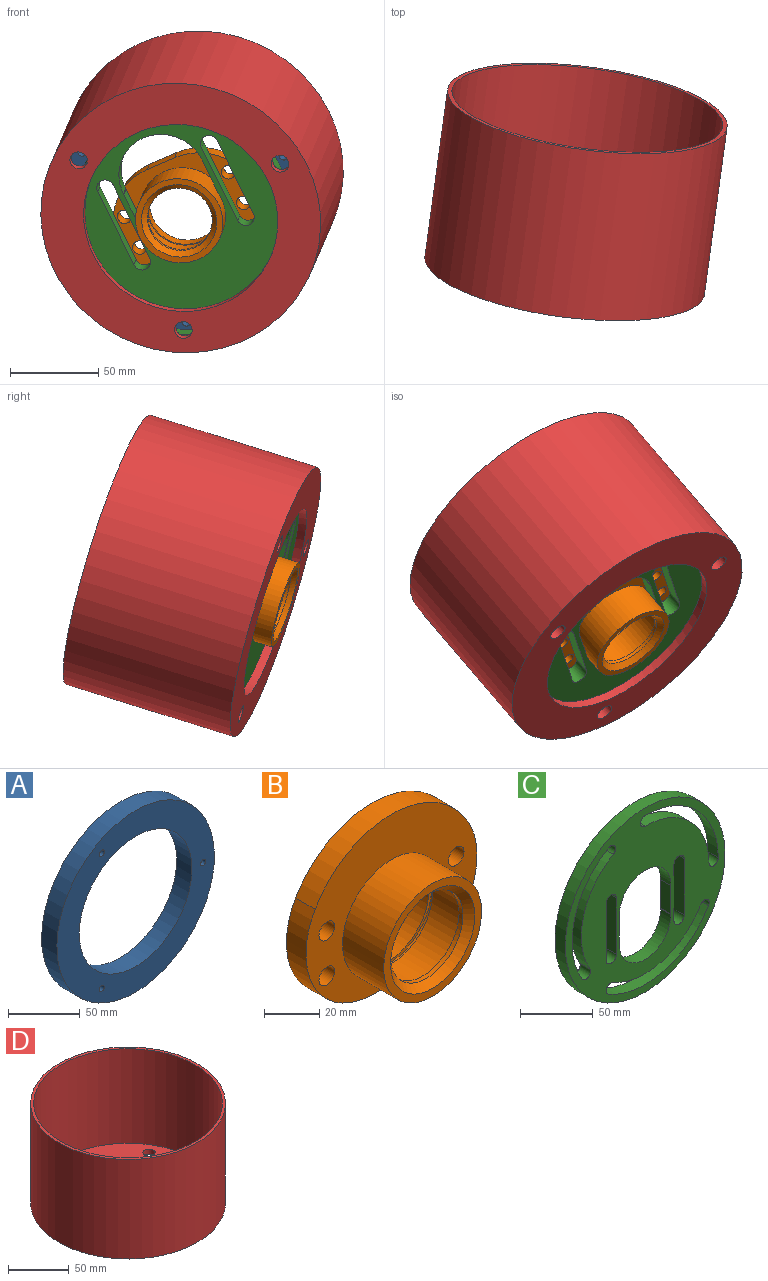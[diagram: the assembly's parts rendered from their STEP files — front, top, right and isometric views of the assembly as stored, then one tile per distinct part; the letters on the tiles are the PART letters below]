
ASSEMBLY  parts=4 mates=4
PART A: 7 faces, bbox 155x15x155 mm
  f0: cylinder r=55.5mm len=111mm, axis (0,1,0), area 5230.8mm2, adj f2,f3
  f1: cylinder r=77.5mm len=155mm, axis (0,1,0), area 7304.2mm2, adj f2,f3
  f2: plane 155x155mm, normal (0,-1,0), area 9133.4mm2, adj f0,f1,f4,f5,f6
  f3: plane 155x155mm, normal (0,1,0), area 9133.4mm2, adj f0,f1,f4,f5,f6
  f4: cylinder r=2.5mm len=15mm, axis (0,1,0), area 235.6mm2, adj f2,f3
  f5: cylinder r=2.5mm len=15mm, axis (0,1,0), area 235.6mm2, adj f2,f3
  f6: cylinder r=2.5mm len=15mm, axis (0,1,0), area 235.6mm2, adj f2,f3
PART B: 20 faces, bbox 87.3x31x75 mm
  f0: plane 87.32x75mm, normal (0,1,0), area 3662.6mm2, adj f1,f11,f12,f13,f14,f15,f17,f18
  f1: cylinder r=45mm len=77.94mm, axis (0,-1,0), area 942.4mm2, adj f0,f2,f18,f19
  f2: plane 87.32x75mm, normal (0,-1,0), area 3084.5mm2, adj f1,f5,f12,f13,f14,f15,f17,f18
  f3: plane 44.5x44.5mm, normal (0,1,0), area 169.8mm2, adj f4,f9
  f4: cylinder r=21mm len=42mm, axis (0,1,0), area 2111.2mm2, adj f3,f6
  f5: cylinder r=25mm len=50mm, axis (0,1,0), area 3298.7mm2, adj f2,f8
  f6: plane 42x42mm, normal (0,1,0), area 310.2mm2, adj f4,f7
  f7: cylinder r=18.5mm len=37mm, axis (0,1,0), area 232.5mm2, adj f6,f16
  f8: plane 50x50mm, normal (0,-1,0), area 511.3mm2, adj f5,f16
  f9: cylinder r=22.25mm len=44.5mm, axis (0,-1,0), area 258.6mm2, adj f3,f10
  f10: plane 44.5x44.5mm, normal (0,-1,0), area 169.8mm2, adj f9,f11
  f11: cylinder r=21mm len=42mm, axis (0,-1,0), area 1075.4mm2, adj f0,f10
  f12: cylinder r=4mm len=10mm, axis (0,-1,0), area 251.3mm2, adj f0,f2
  f13: cylinder r=4mm len=10mm, axis (0,-1,0), area 251.3mm2, adj f0,f2
  f14: cylinder r=4mm len=10mm, axis (0,-1,0), area 251.3mm2, adj f0,f2
  f15: cylinder r=4mm len=10mm, axis (0,-1,0), area 251.3mm2, adj f0,f2
  f16: cone r=18.5mm half-angle=45deg, axis (0,-1,0), area 533.1mm2, adj f7,f8
  f17: plane 17.32x10mm, normal (0,0,-1), area 173.2mm2, adj f0,f2,f18,f19
  f18: cylinder r=35mm len=52.5mm, axis (0,-1,0), area 733mm2, adj f0,f1,f2,f17
  f19: cylinder r=35mm len=52.5mm, axis (0,-1,0), area 733mm2, adj f0,f1,f2,f17
PART C: 29 faces, bbox 155x10x155 mm
  f0: plane 155x155mm, normal (0,-1,0), area 11538.6mm2, adj f2,f3,f4,f5,f6,f7,f8,f9
  f1: plane 155x155mm, normal (0,1,0), area 11538.6mm2, adj f2,f3,f4,f5,f6,f7,f8,f9
  f2: cylinder r=77.5mm len=155mm, axis (0,1,0), area 4869.5mm2, adj f0,f1
  f3: cylinder r=4.5mm len=10mm, axis (0,-1,0), area 141.4mm2, adj f0,f1,f4,f6
  f4: cylinder r=62mm len=62mm, axis (0,-1,0), area 973.9mm2, adj f0,f1,f3,f5
  f5: cylinder r=4.5mm len=10mm, axis (0,-1,0), area 141.4mm2, adj f0,f1,f4,f6
  f6: cylinder r=71mm len=71mm, axis (0,-1,0), area 1115.3mm2, adj f0,f1,f3,f5
  f7: cylinder r=71mm len=96.99mm, axis (0,-1,0), area 1115.3mm2, adj f0,f1,f8,f10
  f8: cylinder r=4.5mm len=10mm, axis (0,-1,0), area 141.4mm2, adj f0,f1,f7,f9
  f9: cylinder r=62mm len=84.69mm, axis (0,-1,0), area 973.9mm2, adj f0,f1,f8,f10
  f10: cylinder r=4.5mm len=10mm, axis (0,-1,0), area 141.4mm2, adj f0,f1,f7,f9
  f11: cylinder r=71mm len=96.99mm, axis (0,-1,0), area 1115.3mm2, adj f0,f1,f12,f14
  f12: cylinder r=4.5mm len=10mm, axis (0,-1,0), area 141.4mm2, adj f0,f1,f11,f13
  f13: cylinder r=62mm len=84.69mm, axis (0,-1,0), area 973.9mm2, adj f0,f1,f12,f14
  f14: cylinder r=4.5mm len=10mm, axis (0,-1,0), area 141.4mm2, adj f0,f1,f11,f13
  f15: cylinder r=25mm len=50mm, axis (0,-1,0), area 791.1mm2, adj f0,f1,f16,f20
  f16: cylinder r=25mm len=10mm, axis (0,-1,0), area 5.8mm2, adj f0,f1,f15,f17
  f17: plane 23.83x10mm, normal (-1,0,0), area 238.3mm2, adj f0,f1,f16,f18
  f18: cylinder r=25mm len=50mm, axis (0,-1,0), area 788.4mm2, adj f0,f1,f17,f19
  f19: plane 23.72x10mm, normal (1,0,0), area 237.2mm2, adj f0,f1,f18,f20
  f20: cylinder r=25mm len=10mm, axis (0,-1,0), area 9.9mm2, adj f0,f1,f15,f19
  f21: plane 47.45x10mm, normal (-1,0,0), area 474.5mm2, adj f0,f1,f22,f24
  f22: cylinder r=5mm len=10mm, axis (0,-1,0), area 157.1mm2, adj f0,f1,f21,f23
  f23: plane 47.45x10mm, normal (1,0,0), area 474.5mm2, adj f0,f1,f22,f24
  f24: cylinder r=5mm len=10mm, axis (0,-1,0), area 157.1mm2, adj f0,f1,f21,f23
  f25: cylinder r=5mm len=10mm, axis (0,-1,0), area 157.1mm2, adj f0,f1,f26,f28
  f26: plane 47.45x10mm, normal (1,0,0), area 474.5mm2, adj f0,f1,f25,f27
  f27: cylinder r=5mm len=10mm, axis (0,-1,0), area 157.1mm2, adj f0,f1,f26,f28
  f28: plane 47.45x10mm, normal (-1,0,0), area 474.5mm2, adj f0,f1,f25,f27
PART D: 9 faces, bbox 160x160x100 mm
  f0: cylinder r=80mm len=160mm, axis (0,0,-1), area 50265.5mm2, adj f1,f2
  f1: plane 160x160mm, normal (0,0,1), area 1237mm2, adj f0,f3
  f2: plane 160x160mm, normal (0,0,-1), area 10193.7mm2, adj f0,f5,f6,f7,f8
  f3: cylinder r=77.5mm len=155mm, axis (0,0,1), area 46260mm2, adj f1,f4
  f4: plane 155x155mm, normal (0,0,1), area 8956.7mm2, adj f3,f5,f6,f7,f8
  f5: cylinder r=55.5mm len=111mm, axis (0,0,-1), area 1743.6mm2, adj f2,f4
  f6: cylinder r=5mm len=10mm, axis (0,0,-1), area 157.1mm2, adj f2,f4
  f7: cylinder r=5mm len=10mm, axis (0,0,-1), area 157.1mm2, adj f2,f4
  f8: cylinder r=5mm len=10mm, axis (0,0,-1), area 157.1mm2, adj f2,f4
PLACE A rot(axis=(0.21,0.97,0.08),91.3deg) t=(-21.88,457.93,266.54)mm
PLACE B rot(axis=(0.1,0.99,0.14),155.6deg) t=(-23.8,443.73,262.11)mm
PLACE C rot(axis=(0.1,0.99,0.14),155.6deg) t=(-23.8,443.73,262.11)mm
PLACE D rot(axis=(0.05,0.59,0.8),174.6deg) t=(-25.64,429.56,257.52)mm fixed
MATE planar C.f18 <-> B.f1  axis (0.13,0.95,0.3) through (-23.8,443.73,262.11)mm
MATE revolute C.f18 <-> A.f1  axis (0.13,0.95,0.3) through (-23.8,443.73,262.11)mm
MATE planar A.f4 <-> D.f7  axis (-0.13,-0.95,-0.3) through (32.63,426.5,292.77)mm
MATE planar A.f5 <-> D.f8  axis (-0.13,-0.95,-0.3) through (-22.47,463.38,198.59)mm
